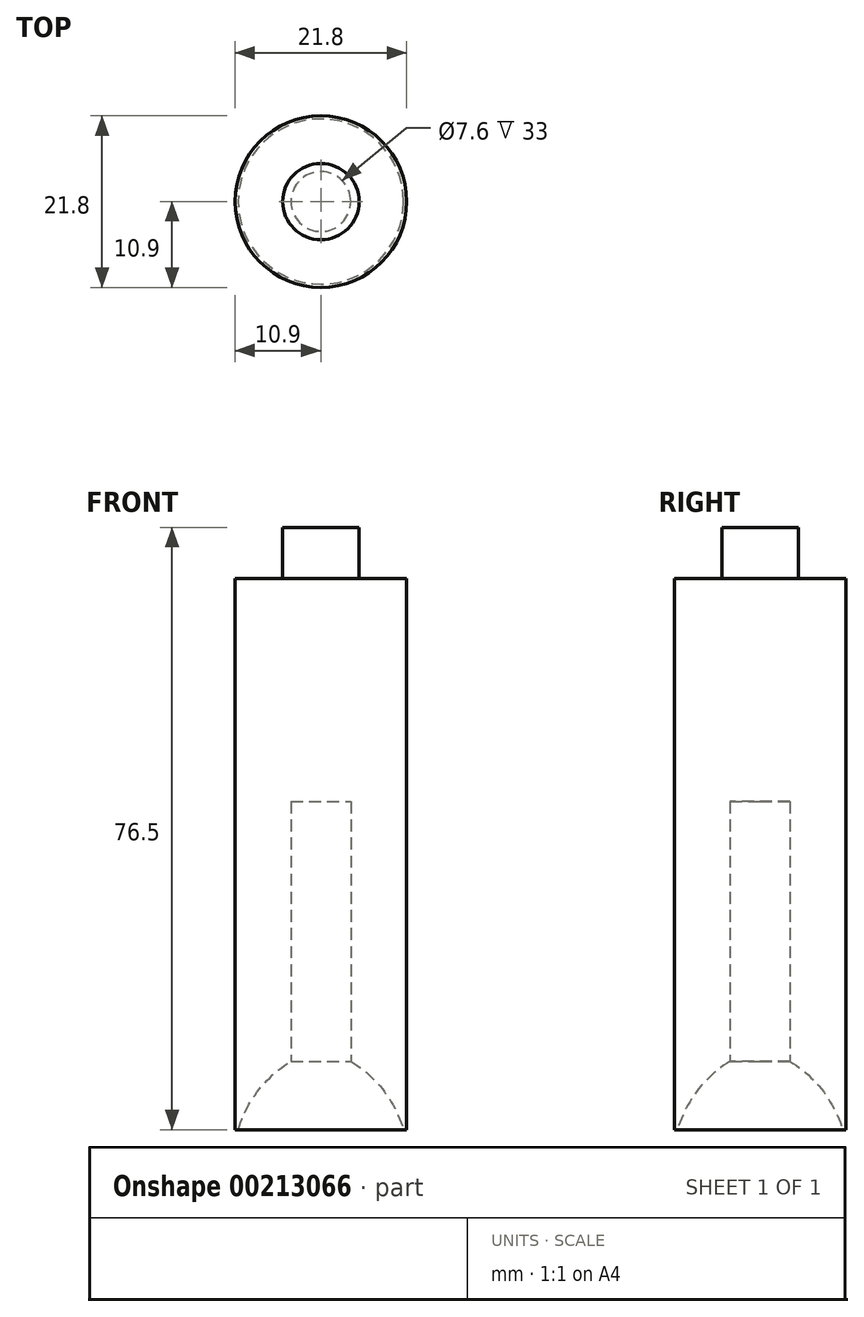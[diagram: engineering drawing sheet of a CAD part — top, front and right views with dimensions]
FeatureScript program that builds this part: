
annotation { "Feature Type Name" : "Feature", "Feature Type Description" : "" }
export const myFeature = defineFeature(function(context is Context, id is Id, definition is map)
    precondition{}
    {
        {
            var Q0;
            Q0=qCreatedBy(makeId("Top.planeOp"),FACE);
            var sketch = newSketch(context, id + "F0", { "sketchPlane" : qUnion([Q0])});
            skCircle(sketch, "E0", {"center": v(0, 0) * mm, "radius": 10.9 * mm});
            skSolve(sketch);
        }
        {
            var Q0;
            Q0=makeQuery(id+"F0.imprint","IMPRINT",FACE,{"disambiguationData":[TD([[makeQuery(id+"F0.imprint","IMPRINT",EDGE,{"derivedFrom":sQuery(id+"F0.wireOp",EDGE,"E0")}),1.0]])]});
            extrude(context, id + "F1", {"entities" : qUnion([Q0]), "depth" : 70 * mm});
        }
        {
            var Q0;
            Q0=qCreatedBy(makeId("Front.planeOp"),FACE);
            var sketch = newSketch(context, id + "F2", { "sketchPlane" : qUnion([Q0])});
            skLineSegment(sketch, "E1", {"start": v(0, 41.7) * mm, "end": v(0, 0) * mm, "construction": true});
            skLineSegment(sketch, "E2", {"start": v(0, 0) * mm, "end": v(0, 41.7) * mm});
            skPoint(sketch, "E3", {"position": v(-28.77, 0) * mm});
            skLineSegment(sketch, "E4", {"start": v(3.8, 8.7) * mm, "end": v(3.8, 41.7) * mm});
            skArc(sketch, "E5", {"start": v(10.5, 0) * mm, "mid": v(7.95, 4.96) * mm, "end": v(3.8, 8.7) * mm});
            skLineSegment(sketch, "E6", {"start": v(0, 41.7) * mm, "end": v(0, 0) * mm});
            skLineSegment(sketch, "E7", {"start": v(0, 0) * mm, "end": v(10.5, 0) * mm});
            skLineSegment(sketch, "E8", {"start": v(0, 41.7) * mm, "end": v(3.8, 41.7) * mm});
            skSolve(sketch);
        }
        {
            var Q0;
            Q0 = qSketchRegion(id + "F2", true);
            var Q1;
            Q1=sQuery(id+"F2.wireOp",EDGE,"E1");
            revolve(context, id + "F3", {"operationType" : NewBodyOperationType.REMOVE, "entities" : qUnion([Q0]), "axis" : qUnion([Q1]), "revolveType" : RevolveType.FULL, "oppositeDirection" : true});
        }
        {
            var Q0;
            Q0=qCreatedBy(makeId("Top.planeOp"),FACE);
            cPlane(context, id + "F4", {"entities" : qUnion([Q0]), "cplaneType" : CPlaneType.OFFSET, "offset" : 70 * mm, "width" : 150 * mm, "height" : 150 * mm});
        }
        {
            var Q0;
            Q0=qCreatedBy(id+"F4.planeOp",FACE);
            var sketch = newSketch(context, id + "F5", { "sketchPlane" : qUnion([Q0])});
            skCircle(sketch, "E9", {"center": v(0, 0) * mm, "radius": 4.85 * mm});
            skSolve(sketch);
        }
        {
            var Q0;
            Q0 = qSketchRegion(id + "F5", true);
            extrude(context, id + "F6", {"entities" : qUnion([Q0]), "operationType" : NewBodyOperationType.ADD, "depth" : 6.5 * mm});
        }
    });
